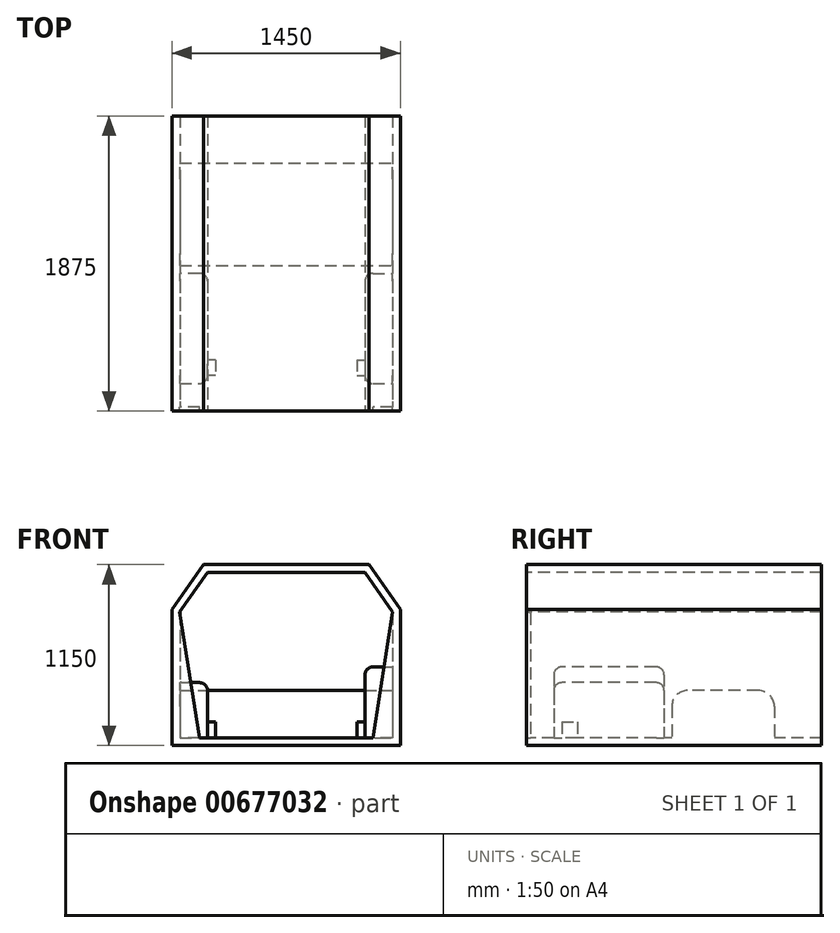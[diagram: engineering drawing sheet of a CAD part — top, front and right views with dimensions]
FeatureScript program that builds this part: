
annotation { "Feature Type Name" : "Feature", "Feature Type Description" : "" }
export const myFeature = defineFeature(function(context is Context, id is Id, definition is map)
    precondition{}
    {
        {
            var Q0;
            Q0=qCreatedBy(makeId("Front.planeOp"),FACE);
            var sketch = newSketch(context, id + "F0", { "sketchPlane" : qUnion([Q0])});
            skLineSegment(sketch, "E0", {"start": v(-175, -250) * mm, "end": v(0, 0) * mm});
            skLineSegment(sketch, "E1", {"start": v(0, 0) * mm, "end": v(500, 0) * mm});
            skLineSegment(sketch, "E2", {"start": v(-175, -250) * mm, "end": v(-175, -1050) * mm});
            skLineSegment(sketch, "E3", {"start": v(-175, -1050) * mm, "end": v(500, -1050) * mm});
            skLineSegment(sketch, "E4", {"start": v(500, -1050) * mm, "end": v(500, 0) * mm, "construction": true});
            skLineSegment(sketch, "E5.MirrorCS", {"start": v(1000, 0) * mm, "end": v(500, 0) * mm});
            skLineSegment(sketch, "E6.MirrorCS", {"start": v(1175, -250) * mm, "end": v(1000, 0) * mm});
            skLineSegment(sketch, "E7.MirrorCS", {"start": v(1175, -250) * mm, "end": v(1175, -1050) * mm});
            skLineSegment(sketch, "E8.MirrorCS", {"start": v(1175, -1050) * mm, "end": v(500, -1050) * mm});
            skLineSegment(sketch, "E9.0", {"start": v(1225, -234.24) * mm, "end": v(1026.03, 50) * mm});
            skLineSegment(sketch, "E9.1", {"start": v(1225, -234.24) * mm, "end": v(1225, -1100) * mm});
            skLineSegment(sketch, "E9.2", {"start": v(1026.03, 50) * mm, "end": v(11.87, 50) * mm});
            skLineSegment(sketch, "E9.3", {"start": v(1225, -1100) * mm, "end": v(0, -1100) * mm});
            skLineSegment(sketch, "E9.4", {"start": v(-26.03, 50) * mm, "end": v(11.87, 50) * mm});
            skLineSegment(sketch, "E9.5", {"start": v(-225, -234.24) * mm, "end": v(-26.03, 50) * mm});
            skLineSegment(sketch, "E9.6", {"start": v(-225, -234.24) * mm, "end": v(-225, -1100) * mm});
            skLineSegment(sketch, "E9.7", {"start": v(-225, -1100) * mm, "end": v(0, -1100) * mm});
            skSolve(sketch);
        }
        {
            var Q0;
            Q0 = qSketchRegion(id + "F0", true);
            extrude(context, id + "F1", {"entities" : qUnion([Q0]), "oppositeDirection" : true, "depth" : 1850 * mm, "offsetDistance" : 25 * mm});
        }
        {
            var Q0;
            Q0=makeQuery(id+"F1.opExtrude","SWEPT_FACE",FACE,{"disambiguationData":[OSD([sQuery(id+"F0.wireOp",EDGE,"E3"),sQuery(id+"F0.wireOp",EDGE,"E8.MirrorCS")])]});
            var sketch = newSketch(context, id + "F2", { "sketchPlane" : qUnion([Q0])});
            skLineSegment(sketch, "E10", {"start": v(500, 1550) * mm, "end": v(500, 0) * mm, "construction": true});
            skLineSegment(sketch, "E11", {"start": v(0, 850) * mm, "end": v(0, 150) * mm});
            skLineSegment(sketch, "E12", {"start": v(1000, 850) * mm, "end": v(1000, 150) * mm});
            skLineSegment(sketch, "E13.bottom", {"start": v(-175, 1550) * mm, "end": v(1175, 1550) * mm});
            skLineSegment(sketch, "E13.top", {"start": v(-175, 900) * mm, "end": v(1175, 900) * mm});
            skLineSegment(sketch, "E13.left", {"start": v(-175, 1550) * mm, "end": v(-175, 900) * mm});
            skLineSegment(sketch, "E13.right", {"start": v(1175, 1550) * mm, "end": v(1175, 900) * mm});
            skLineSegment(sketch, "E14", {"start": v(0, 850) * mm, "end": v(-175, 850) * mm});
            skLineSegment(sketch, "E15", {"start": v(1000, 850) * mm, "end": v(1175, 850) * mm});
            skLineSegment(sketch, "E16", {"start": v(-175, 850) * mm, "end": v(-175, 150) * mm});
            skLineSegment(sketch, "E17", {"start": v(1175, 850) * mm, "end": v(1175, 150) * mm});
            skLineSegment(sketch, "E18", {"start": v(-175, 150) * mm, "end": v(0, 150) * mm});
            skLineSegment(sketch, "E19", {"start": v(1000, 150) * mm, "end": v(1175, 150) * mm});
            skSolve(sketch);
        }
        {
            var Q0;
            Q0=makeQuery(id+"F2.imprint","IMPRINT",FACE,{"disambiguationData":[TD([[makeQuery(id+"F2.imprint","IMPRINT",EDGE,{"derivedFrom":sQuery(id+"F2.wireOp",EDGE,"E11")}),-1.0]])]});
            extrude(context, id + "F3", {"entities" : qUnion([Q0]), "operationType" : NewBodyOperationType.ADD, "depth" : 350 * mm, "offsetDistance" : 25 * mm});
        }
        {
            var Q0;
            {var subQ0=sQuery(id+"F2.wireOp",EDGE,"8c420d4a-1429-4711-9b67-bd08c4f59354.MirrorCS");Q0=makeQuery(id+"F2.imprint","IMPRINT",FACE,{"disambiguationData":[TD([[makeQuery(id+"F2.imprint","IMPRINT",EDGE,{"derivedFrom":subQ0}),-1.0]])]});}
            var Q1;
            Q1=makeQuery(id+"F2.imprint","IMPRINT",FACE,{"disambiguationData":[TD([[makeQuery(id+"F2.imprint","IMPRINT",EDGE,{"derivedFrom":sQuery(id+"F2.wireOp",EDGE,"E12")}),1.0]])]});
            extrude(context, id + "F4", {"entities" : qUnion([Q0, Q1]), "operationType" : NewBodyOperationType.ADD, "depth" : 450 * mm, "offsetDistance" : 25 * mm});
        }
        {
            var Q0;
            Q0=makeQuery(id+"F3.opExtrude","SWEPT_FACE",FACE,{"disambiguationData":[OSD([sQuery(id+"F2.wireOp",EDGE,"E11")])]});
            var sketch = newSketch(context, id + "F5", { "sketchPlane" : qUnion([Q0])});
            skLineSegment(sketch, "E20.bottom", {"start": v(200, -950) * mm, "end": v(300, -950) * mm});
            skLineSegment(sketch, "E20.top", {"start": v(200, -1050) * mm, "end": v(300, -1050) * mm});
            skLineSegment(sketch, "E20.left", {"start": v(200, -950) * mm, "end": v(200, -1050) * mm});
            skLineSegment(sketch, "E20.right", {"start": v(300, -950) * mm, "end": v(300, -1050) * mm});
            skSolve(sketch);
        }
        {
            var Q0;
            Q0=makeQuery(id+"F5.imprint","IMPRINT",FACE,{"disambiguationData":[TD([[makeQuery(id+"F5.imprint","IMPRINT",EDGE,{"derivedFrom":sQuery(id+"F5.wireOp",EDGE,"E20.bottom")}),-1.0]])]});
            extrude(context, id + "F6", {"entities" : qUnion([Q0]), "operationType" : NewBodyOperationType.ADD, "depth" : 50 * mm, "offsetDistance" : 25 * mm});
        }
        {
            var Q0;
            Q0=makeQuery(id+"F4.opExtrude","SWEPT_FACE",FACE,{"disambiguationData":[OSD([sQuery(id+"F2.wireOp",EDGE,"E12")])]});
            var sketch = newSketch(context, id + "F7", { "sketchPlane" : qUnion([Q0])});
            skLineSegment(sketch, "E21.bottom", {"start": v(-300, -1050) * mm, "end": v(-200, -1050) * mm});
            skLineSegment(sketch, "E21.top", {"start": v(-300, -950) * mm, "end": v(-200, -950) * mm});
            skLineSegment(sketch, "E21.left", {"start": v(-300, -1050) * mm, "end": v(-300, -950) * mm});
            skLineSegment(sketch, "E21.right", {"start": v(-200, -1050) * mm, "end": v(-200, -950) * mm});
            skSolve(sketch);
        }
        {
            var Q0;
            Q0 = qSketchRegion(id + "F7", true);
            extrude(context, id + "F8", {"entities" : qUnion([Q0]), "operationType" : NewBodyOperationType.ADD, "depth" : 50 * mm, "offsetDistance" : 25 * mm});
        }
        {
            var Q0;
            Q0=makeQuery(id+"F3.opExtrude","CAP_EDGE",EDGE,{"disambiguationData":[OSD([sQuery(id+"F2.wireOp",EDGE,"75b1485a-da66-413b-9641-59c65db2b8ac")])],"isStart":false});
            var Q1;
            Q1=makeQuery(id+"F3.opExtrude","CAP_EDGE",EDGE,{"disambiguationData":[OSD([sQuery(id+"F0.wireOp",EDGE,"E3"),sQuery(id+"F0.wireOp",EDGE,"E8.MirrorCS")])],"isStart":false});
            var Q2;
            Q2=makeQuery(id+"F3.opExtrude","CAP_EDGE",EDGE,{"disambiguationData":[OSD([sQuery(id+"F2.wireOp",EDGE,"0cde3d60-4009-49fa-b9cd-9c3c3415403f")])],"isStart":false});
            var Q3;
            Q3=makeQuery(id+"F3.opExtrude","CAP_FACE",FACE,{"disambiguationData":[OSD([sQuery(id+"F0.wireOp",EDGE,"E3"),sQuery(id+"F0.wireOp",EDGE,"E8.MirrorCS"),sQuery(id+"F2.wireOp",EDGE,"54d70378-253d-4027-86a2-24b1ebb3a17b"),sQuery(id+"F2.wireOp",EDGE,"75b1485a-da66-413b-9641-59c65db2b8ac"),sQuery(id+"F2.wireOp",EDGE,"0cde3d60-4009-49fa-b9cd-9c3c3415403f")])],"isStart":false});
            var Q4;
            Q4=makeQuery(id+"F4.opExtrude","CAP_EDGE",EDGE,{"disambiguationData":[OSD([sQuery(id+"F2.wireOp",EDGE,"3db89c7a-6986-4e41-bff7-ecd04f6990a2.MirrorCS")])],"isStart":false});
            var Q5;
            Q5=makeQuery(id+"F4.opExtrude","CAP_FACE",FACE,{"disambiguationData":[OSD([sQuery(id+"F0.wireOp",EDGE,"E3"),sQuery(id+"F0.wireOp",EDGE,"E7.MirrorCS"),sQuery(id+"F0.wireOp",EDGE,"E8.MirrorCS"),sQuery(id+"F2.wireOp",EDGE,"8c420d4a-1429-4711-9b67-bd08c4f59354.MirrorCS"),sQuery(id+"F2.wireOp",EDGE,"3db89c7a-6986-4e41-bff7-ecd04f6990a2.MirrorCS")])],"isStart":false});
            var Q6;
            Q6=makeQuery(id+"F3.opExtrude","SWEPT_EDGE",EDGE,{"disambiguationData":[OSD([sQuery(id+"F0.wireOp",EDGE,"E3"),sQuery(id+"F0.wireOp",EDGE,"E8.MirrorCS"),sQuery(id+"F2.wireOp",EDGE,"96869249-ad9b-46ec-be2c-cb1e5d1da1af"),sQuery(id+"F2.wireOp",EDGE,"75b1485a-da66-413b-9641-59c65db2b8ac")])]});
            var Q7;
            Q7=makeQuery(id+"F3.opExtrude","SWEPT_EDGE",EDGE,{"disambiguationData":[OSD([sQuery(id+"F2.wireOp",EDGE,"E11"),sQuery(id+"F2.wireOp",EDGE,"75b1485a-da66-413b-9641-59c65db2b8ac"),sQuery(id+"F2.wireOp",EDGE,"0cde3d60-4009-49fa-b9cd-9c3c3415403f")])]});
            var Q8;
            Q8=makeQuery(id+"F4.opExtrude","SWEPT_EDGE",EDGE,{"disambiguationData":[OSD([sQuery(id+"F0.wireOp",EDGE,"E3"),sQuery(id+"F0.wireOp",EDGE,"E8.MirrorCS"),sQuery(id+"F2.wireOp",EDGE,"96869249-ad9b-46ec-be2c-cb1e5d1da1af"),sQuery(id+"F2.wireOp",EDGE,"3db89c7a-6986-4e41-bff7-ecd04f6990a2.MirrorCS")])]});
            var Q9;
            Q9=makeQuery(id+"F4.opExtrude","SWEPT_EDGE",EDGE,{"disambiguationData":[OSD([sQuery(id+"F2.wireOp",EDGE,"E12"),sQuery(id+"F2.wireOp",EDGE,"8c420d4a-1429-4711-9b67-bd08c4f59354.MirrorCS"),sQuery(id+"F2.wireOp",EDGE,"3db89c7a-6986-4e41-bff7-ecd04f6990a2.MirrorCS")])]});
            var Q10;
            Q10=makeQuery(id+"F3.opExtrude","CAP_EDGE",EDGE,{"disambiguationData":[OSD([sQuery(id+"F2.wireOp",EDGE,"E11")])],"isStart":false});
            var Q11;
            Q11=makeQuery(id+"F3.opExtrude","CAP_EDGE",EDGE,{"disambiguationData":[OSD([sQuery(id+"F2.wireOp",EDGE,"E18")])],"isStart":false});
            var Q12;
            Q12=makeQuery(id+"F3.opExtrude","CAP_EDGE",EDGE,{"disambiguationData":[OSD([sQuery(id+"F2.wireOp",EDGE,"E14")])],"isStart":false});
            var Q13;
            Q13=makeQuery(id+"F4.opExtrude","CAP_EDGE",EDGE,{"disambiguationData":[OSD([sQuery(id+"F2.wireOp",EDGE,"E19")])],"isStart":false});
            var Q14;
            Q14=makeQuery(id+"F4.opExtrude","CAP_EDGE",EDGE,{"disambiguationData":[OSD([sQuery(id+"F2.wireOp",EDGE,"E12")])],"isStart":false});
            var Q15;
            Q15=makeQuery(id+"F4.opExtrude","CAP_EDGE",EDGE,{"disambiguationData":[OSD([sQuery(id+"F2.wireOp",EDGE,"E15")])],"isStart":false});
            fillet(context, id + "F9", {"entities" : qUnion([Q0, Q1, Q2, Q3, Q4, Q5, Q6, Q7, Q8, Q9, Q10, Q11, Q12, Q13, Q14, Q15]), "radius" : 50 * mm, "tangentPropagation" : true, "allowEdgeOverflow" : false});
        }
        {
            var Q0;
            Q0=makeQuery(id+"F2.imprint","IMPRINT",FACE,{"disambiguationData":[TD([[makeQuery(id+"F2.imprint","IMPRINT",EDGE,{"derivedFrom":sQuery(id+"F2.wireOp",EDGE,"E13.bottom")}),-1.0]])]});
            extrude(context, id + "F10", {"entities" : qUnion([Q0]), "operationType" : NewBodyOperationType.ADD, "depth" : 300 * mm, "offsetDistance" : 25 * mm});
        }
        {
            var Q0;
            Q0=makeQuery(id+"F10.opExtrude","CAP_EDGE",EDGE,{"disambiguationData":[OSD([sQuery(id+"F2.wireOp",EDGE,"E13.top")])],"isStart":false});
            var Q1;
            Q1=makeQuery(id+"F10.opExtrude","CAP_EDGE",EDGE,{"disambiguationData":[OSD([sQuery(id+"F2.wireOp",EDGE,"E13.bottom")])],"isStart":false});
            fillet(context, id + "F11", {"entities" : qUnion([Q0, Q1]), "radius" : 100 * mm, "tangentPropagation" : true, "allowEdgeOverflow" : false});
        }
        {
            var Q0;
            {var subQ0=sQuery(id+"F0.wireOp",EDGE,"E8.MirrorCS");var subQ1=sQuery(id+"F0.wireOp",EDGE,"E3");Q0=makeQuery(id+"F9.opFillet","SPLIT",FACE,{"disambiguationData":[OD(0.0)],"derivedFrom":makeQuery(id+"F4.boolean.opBoolean","MERGE",FACE,{"derivedFrom":[makeQuery(id+"F3.boolean.opBoolean","MERGE",FACE,{"derivedFrom":[makeQuery(id+"F1.opExtrude","CAP_FACE",FACE,{"disambiguationData":[OSD([sQuery(id+"F0.wireOp",EDGE,"E0"),sQuery(id+"F0.wireOp",EDGE,"E1"),sQuery(id+"F0.wireOp",EDGE,"E2"),subQ1,sQuery(id+"F0.wireOp",EDGE,"E5.MirrorCS"),sQuery(id+"F0.wireOp",EDGE,"E6.MirrorCS"),sQuery(id+"F0.wireOp",EDGE,"E7.MirrorCS"),subQ0,sQuery(id+"F0.wireOp",EDGE,"E9.0"),sQuery(id+"F0.wireOp",EDGE,"E9.1"),sQuery(id+"F0.wireOp",EDGE,"E9.2"),sQuery(id+"F0.wireOp",EDGE,"E9.3"),sQuery(id+"F0.wireOp",EDGE,"E9.4"),sQuery(id+"F0.wireOp",EDGE,"E9.5"),sQuery(id+"F0.wireOp",EDGE,"E9.6"),sQuery(id+"F0.wireOp",EDGE,"E9.7")])],"isStart":true}),makeQuery(id+"F3.opExtrude","SWEPT_FACE",FACE,{"disambiguationData":[OSD([subQ1,subQ0])]})]}),makeQuery(id+"F4.opExtrude","SWEPT_FACE",FACE,{"disambiguationData":[OSD([subQ1,subQ0])]})]})});}
            var sketch = newSketch(context, id + "F12", { "sketchPlane" : qUnion([Q0])});
            skLineSegment(sketch, "E22", {"start": v(-50, -1050) * mm, "end": v(1050, -1050) * mm});
            skLineSegment(sketch, "E23", {"start": v(1050, -1050) * mm, "end": v(1176.24, -251.78) * mm});
            skLineSegment(sketch, "E24", {"start": v(1176.24, -251.78) * mm, "end": v(1000, 0) * mm});
            skLineSegment(sketch, "E25", {"start": v(1000, 0) * mm, "end": v(0, 0) * mm});
            skLineSegment(sketch, "E26", {"start": v(0, 0) * mm, "end": v(-176.24, -251.78) * mm});
            skLineSegment(sketch, "E27", {"start": v(-176.24, -251.78) * mm, "end": v(-50, -1050) * mm});
            skLineSegment(sketch, "E28", {"start": v(-225, -234.24) * mm, "end": v(-225, -1100) * mm});
            skLineSegment(sketch, "E29", {"start": v(-225, -1100) * mm, "end": v(1225, -1100) * mm});
            skLineSegment(sketch, "E30", {"start": v(1225, -1100) * mm, "end": v(1225, -234.24) * mm});
            skLineSegment(sketch, "E31", {"start": v(1225, -234.24) * mm, "end": v(1026.03, 50) * mm});
            skLineSegment(sketch, "E32", {"start": v(1026.03, 50) * mm, "end": v(-26.03, 50) * mm});
            skLineSegment(sketch, "E33", {"start": v(-26.03, 50) * mm, "end": v(-225, -234.24) * mm});
            skSolve(sketch);
        }
        {
            var Q0;
            Q0 = qSketchRegion(id + "F12", true);
            extrude(context, id + "F13", {"entities" : qUnion([Q0]), "operationType" : NewBodyOperationType.ADD, "depth" : 25 * mm, "offsetDistance" : 25 * mm});
        }
    });
